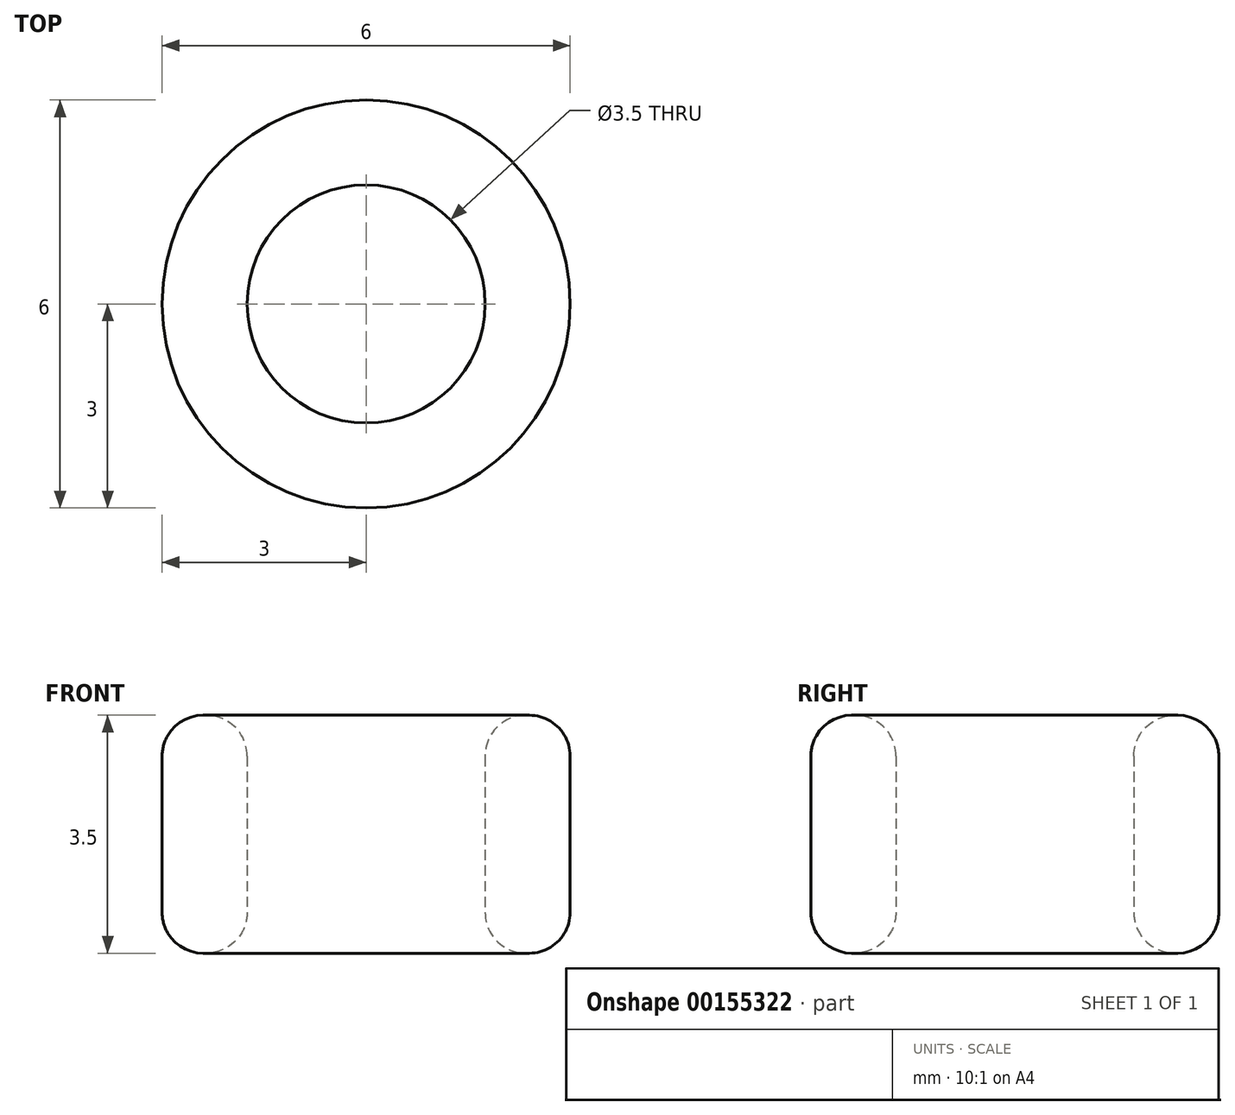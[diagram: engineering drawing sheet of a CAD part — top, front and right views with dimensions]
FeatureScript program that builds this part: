
annotation { "Feature Type Name" : "Feature", "Feature Type Description" : "" }
export const myFeature = defineFeature(function(context is Context, id is Id, definition is map)
    precondition{}
    {
        {
            var Q0;
            Q0=qCreatedBy(makeId("Top.planeOp"),FACE);
            var sketch = newSketch(context, id + "F0", { "sketchPlane" : qUnion([Q0])});
            skCircle(sketch, "E0", {"center": v(0, 0) * mm, "radius": 1.75 * mm});
            skCircle(sketch, "E1", {"center": v(0, 0) * mm, "radius": 3 * mm});
            skSolve(sketch);
        }
        {
            var Q0;
            Q0=qSketchRegion(id+"F0",true);
            extrude(context, id + "F1", {"entities" : qUnion([Q0]), "depth" : 3.5 * mm});
        }
        {
            var Q0;
            Q0=makeQuery(id+"F1.opExtrude","CAP_EDGE",EDGE,{"disambiguationData":[OSD([sQuery(id+"F0.wireOp",EDGE,"E1")])],"isStart":false});
            var Q1;
            Q1=makeQuery(id+"F1.opExtrude","CAP_EDGE",EDGE,{"disambiguationData":[OSD([sQuery(id+"F0.wireOp",EDGE,"E0")])],"isStart":false});
            var Q2;
            Q2=makeQuery(id+"F1.opExtrude","CAP_EDGE",EDGE,{"disambiguationData":[OSD([sQuery(id+"F0.wireOp",EDGE,"E1")])],"isStart":true});
            var Q3;
            Q3=makeQuery(id+"F1.opExtrude","CAP_EDGE",EDGE,{"disambiguationData":[OSD([sQuery(id+"F0.wireOp",EDGE,"E0")])],"isStart":true});
            fillet(context, id + "F2", {"entities" : qUnion([Q0, Q1, Q2, Q3]), "radius" : 0.6 * mm, "tangentPropagation" : true, "allowEdgeOverflow" : false});
        }
    });
